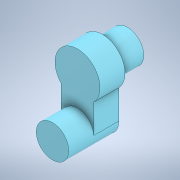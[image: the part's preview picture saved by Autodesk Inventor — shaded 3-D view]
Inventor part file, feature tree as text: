
AUTODESK INVENTOR PART (.ipt)
format: ipt  version: 2022 (Build 260153000, 153)  size: 133,632 bytes
history: native  units: in
note: dims shown in document units (in); Inventor stores cm internally (conversion verified against a paired STEP export)
features: extrude x3, sketch x2
ambient origin geometry x8: Origin, YZ Plane, XZ Plane, XY Plane, X Axis, Y Axis, Z Axis, Center Point
bodies: Solid1 (feature_tree)
feature tree (5):
  sketch  "Sketch2"  dims[d0=0.1969in d1=0.0in d2=0.1969in d3=0.0in]
  extrude  "Extrusion1"  Depth=0.1969in TaperAngle=0.0deg
  extrude  "Extrusion2"  Depth=0.1969in
  extrude  "Extrusion3"  Depth=0.1969in
  sketch  "Sketch3"  dims[d4=0.1969in d5=0.0in d6=0.2559in d7=0.3543in d8=0.3543in]
